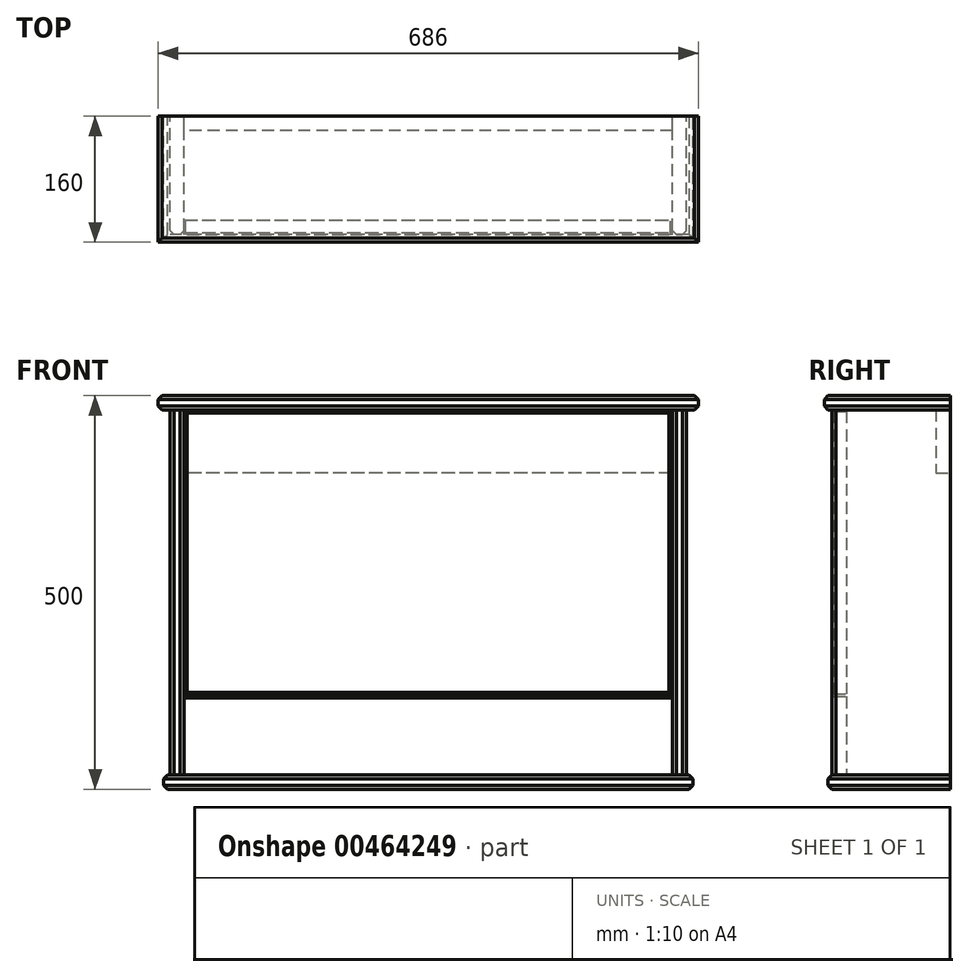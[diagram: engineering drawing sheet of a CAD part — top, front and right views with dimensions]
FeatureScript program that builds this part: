
annotation { "Feature Type Name" : "Feature", "Feature Type Description" : "" }
export const myFeature = defineFeature(function(context is Context, id is Id, definition is map)
    precondition{}
    {
        {
            assignVariable(context, id + "F0", {"name" : "wood", "anyValue" : 18});
        }
        {
            var Q0;
            Q0=qCreatedBy(makeId("Front.planeOp"),FACE);
            var sketch = newSketch(context, id + "F1", { "sketchPlane" : qUnion([Q0])});
            skLineSegment(sketch, "E0.bottom", {"start": v(-310, 482) * mm, "end": v(310, 482) * mm});
            skLineSegment(sketch, "E0.top", {"start": v(-310, 18) * mm, "end": v(310, 18) * mm});
            skLineSegment(sketch, "E0.left", {"start": v(-310, 482) * mm, "end": v(-310, 18) * mm});
            skLineSegment(sketch, "E0.right", {"start": v(310, 482) * mm, "end": v(310, 18) * mm});
            skLineSegment(sketch, "E1.bottom", {"start": v(-328, 500) * mm, "end": v(328, 500) * mm});
            skLineSegment(sketch, "E1.top", {"start": v(-328, 0) * mm, "end": v(328, 0) * mm});
            skLineSegment(sketch, "E1.left", {"start": v(-328, 482) * mm, "end": v(-328, 18) * mm});
            skLineSegment(sketch, "E1.right", {"start": v(328, 482) * mm, "end": v(328, 18) * mm});
            skLineSegment(sketch, "E2", {"start": v(-310, 482) * mm, "end": v(-328, 482) * mm});
            skLineSegment(sketch, "E3", {"start": v(310, 482) * mm, "end": v(328, 482) * mm});
            skLineSegment(sketch, "E4", {"start": v(-310, 18) * mm, "end": v(-328, 18) * mm});
            skLineSegment(sketch, "E5", {"start": v(310, 18) * mm, "end": v(328, 18) * mm});
            skLineSegment(sketch, "E6", {"start": v(-310, 118) * mm, "end": v(310, 118) * mm});
            skPoint(sketch, "E7.oppositeSnap0", {"position": v(319, 482) * mm});
            skLineSegment(sketch, "E7.bottom", {"start": v(328, 500) * mm, "end": v(343, 500) * mm});
            skLineSegment(sketch, "E7.top", {"start": v(328, 482) * mm, "end": v(343, 482) * mm});
            skLineSegment(sketch, "E7.right", {"start": v(343, 500) * mm, "end": v(343, 482) * mm});
            skLineSegment(sketch, "E8.MirrorCS", {"start": v(-328, 482) * mm, "end": v(-343, 482) * mm});
            skLineSegment(sketch, "E9.MirrorCS", {"start": v(-343, 500) * mm, "end": v(-343, 482) * mm});
            skLineSegment(sketch, "E10.MirrorCS", {"start": v(-328, 500) * mm, "end": v(-343, 500) * mm});
            skLineSegment(sketch, "E11", {"start": v(328, 18) * mm, "end": v(336, 18) * mm});
            skLineSegment(sketch, "E12", {"start": v(336, 18) * mm, "end": v(336, 0) * mm});
            skLineSegment(sketch, "E13", {"start": v(336, 0) * mm, "end": v(328, 0) * mm});
            skLineSegment(sketch, "E14.MirrorCS", {"start": v(-328, 18) * mm, "end": v(-336, 18) * mm});
            skLineSegment(sketch, "E15.MirrorCS", {"start": v(-336, 0) * mm, "end": v(-328, 0) * mm});
            skLineSegment(sketch, "E16.MirrorCS", {"start": v(-336, 18) * mm, "end": v(-336, 0) * mm});
            skLineSegment(sketch, "E17.bottom", {"start": v(-308, 480) * mm, "end": v(308, 480) * mm});
            skLineSegment(sketch, "E17.top", {"start": v(-308, 121) * mm, "end": v(308, 121) * mm});
            skLineSegment(sketch, "E17.left", {"start": v(-308, 480) * mm, "end": v(-308, 121) * mm});
            skLineSegment(sketch, "E17.right", {"start": v(308, 480) * mm, "end": v(308, 121) * mm});
            skSolve(sketch);
        }
        {
            var Q0;
            {var subQ0=sQuery(id+"F1.wireOp",EDGE,"E2");Q0=makeQuery(id+"F1.imprint","IMPRINT",FACE,{"disambiguationData":[TD([[makeQuery(id+"F1.imprint","IMPRINT",EDGE,{"derivedFrom":subQ0}),1.0]])]});}
            var Q1;
            Q1=makeQuery(id+"F1.imprint","IMPRINT",FACE,{"disambiguationData":[TD([[makeQuery(id+"F1.imprint","IMPRINT",EDGE,{"derivedFrom":sQuery(id+"F1.wireOp",EDGE,"E1.right")}),-1.0]])]});
            extrude(context, id + "F2", {"entities" : qUnion([Q0, Q1]), "depth" : 150 * mm, "offsetDistance" : 25 * mm});
        }
        {
            var Q0;
            Q0=makeQuery(id+"F1.imprint","IMPRINT",FACE,{"disambiguationData":[TD([[makeQuery(id+"F1.imprint","IMPRINT",EDGE,{"derivedFrom":sQuery(id+"F1.wireOp",EDGE,"E0.top")}),-1.0]])]});
            var Q1;
            Q1=makeQuery(id+"F2.opExtrude","CAP_FACE",FACE,{"disambiguationData":[OSD([sQuery(id+"F1.wireOp",EDGE,"E0.left"),sQuery(id+"F1.wireOp",EDGE,"E1.left"),sQuery(id+"F1.wireOp",EDGE,"E2"),sQuery(id+"F1.wireOp",EDGE,"E4")])],"isStart":false});
            extrude(context, id + "F3", {"entities" : qUnion([Q0]), "endBound" : BoundingType.UP_TO_SURFACE, "depth" : 25 * mm, "endBoundEntityFace" : qUnion([Q1]), "hasOffset" : true, "offsetDistance" : 5 * mm, "offsetOppositeDirection" : true});
        }
        {
            var Q0;
            {var subQ0=sQuery(id+"F1.wireOp",EDGE,"E0.top");Q0=makeQuery(id+"F1.imprint","IMPRINT",FACE,{"disambiguationData":[TD([[makeQuery(id+"F1.imprint","IMPRINT",EDGE,{"derivedFrom":subQ0}),1.0]])]});}
            var Q1;
            Q1=makeQuery(id+"F2.opExtrude","CAP_FACE",FACE,{"disambiguationData":[OSD([sQuery(id+"F1.wireOp",EDGE,"E0.left"),sQuery(id+"F1.wireOp",EDGE,"E1.left"),sQuery(id+"F1.wireOp",EDGE,"E2"),sQuery(id+"F1.wireOp",EDGE,"E4")])],"isStart":false});
            var Q2;
            Q2=makeQuery(id+"F2.opExtrude","CAP_FACE",FACE,{"disambiguationData":[OSD([sQuery(id+"F1.wireOp",EDGE,"E0.left"),sQuery(id+"F1.wireOp",EDGE,"E1.left"),sQuery(id+"F1.wireOp",EDGE,"E2"),sQuery(id+"F1.wireOp",EDGE,"E4")])],"isStart":false});
            extrude(context, id + "F4", {"entities" : qUnion([Q0]), "endBound" : BoundingType.UP_TO_SURFACE, "depth" : 25 * mm, "endBoundEntityFace" : qUnion([Q1]), "offsetDistance" : 25 * mm, "hasSecondDirection" : true, "secondDirectionBound" : BoundingType.UP_TO_SURFACE, "secondDirectionOppositeDirection" : false, "secondDirectionDepth" : 25 * mm, "secondDirectionBoundEntityFace" : qUnion([Q2]), "hasSecondDirectionOffset" : true, "secondDirectionOffsetDistance" : (getVariable(context, 'wood')) * mm});
        }
        {
            var Q0;
            Q0=makeQuery(id+"F1.imprint","IMPRINT",FACE,{"disambiguationData":[TD([[makeQuery(id+"F1.imprint","IMPRINT",EDGE,{"derivedFrom":sQuery(id+"F1.wireOp",EDGE,"E0.bottom")}),1.0]])]});
            var Q1;
            Q1=makeQuery(id+"F2.opExtrude","CAP_FACE",FACE,{"disambiguationData":[OSD([sQuery(id+"F1.wireOp",EDGE,"E0.left"),sQuery(id+"F1.wireOp",EDGE,"E1.left"),sQuery(id+"F1.wireOp",EDGE,"E2"),sQuery(id+"F1.wireOp",EDGE,"E4")])],"isStart":false});
            extrude(context, id + "F5", {"entities" : qUnion([Q0]), "endBound" : BoundingType.UP_TO_SURFACE, "depth" : 25 * mm, "endBoundEntityFace" : qUnion([Q1]), "hasOffset" : true, "offsetDistance" : 10 * mm, "offsetOppositeDirection" : true});
        }
        {
            var Q0;
            Q0=makeQuery(id+"F1.imprint","IMPRINT",FACE,{"disambiguationData":[TD([[makeQuery(id+"F1.imprint","IMPRINT",EDGE,{"derivedFrom":sQuery(id+"F1.wireOp",EDGE,"E17.bottom")}),-1.0]])]});
            var Q1;
            Q1=makeQuery(id+"F4.opExtrude","CAP_FACE",FACE,{"disambiguationData":[OSD([sQuery(id+"F1.wireOp",EDGE,"E0.top"),sQuery(id+"F1.wireOp",EDGE,"E0.left"),sQuery(id+"F1.wireOp",EDGE,"E0.right"),sQuery(id+"F1.wireOp",EDGE,"E6")])],"isStart":false});
            var Q2;
            Q2=makeQuery(id+"F4.opExtrude","CAP_FACE",FACE,{"disambiguationData":[OSD([sQuery(id+"F1.wireOp",EDGE,"E0.top"),sQuery(id+"F1.wireOp",EDGE,"E0.left"),sQuery(id+"F1.wireOp",EDGE,"E0.right"),sQuery(id+"F1.wireOp",EDGE,"E6")])],"isStart":false});
            extrude(context, id + "F6", {"entities" : qUnion([Q0]), "endBound" : BoundingType.UP_TO_SURFACE, "depth" : (getVariable(context, 'wood')) * mm, "endBoundEntityFace" : qUnion([Q1]), "offsetDistance" : (getVariable(context, 'wood')) * mm, "offsetOppositeDirection" : true, "hasSecondDirection" : true, "secondDirectionBound" : BoundingType.UP_TO_SURFACE, "secondDirectionOppositeDirection" : false, "secondDirectionDepth" : 25 * mm, "secondDirectionBoundEntityFace" : qUnion([Q2]), "hasSecondDirectionOffset" : true, "secondDirectionOffsetDistance" : (getVariable(context, 'wood')) * mm});
        }
        {
            var Q0;
            Q0=makeQuery(id+"F1.imprint","IMPRINT",FACE,{"disambiguationData":[TD([[makeQuery(id+"F1.imprint","IMPRINT",EDGE,{"derivedFrom":sQuery(id+"F1.wireOp",EDGE,"E17.bottom")}),-1.0]])]});
            var sketch = newSketch(context, id + "F7", { "sketchPlane" : qUnion([Q0])});
            skLineSegment(sketch, "E18.bottom", {"start": v(310, 482) * mm, "end": v(-310, 482) * mm});
            skLineSegment(sketch, "E18.top", {"start": v(310, 402) * mm, "end": v(-310, 402) * mm});
            skLineSegment(sketch, "E18.left", {"start": v(310, 482) * mm, "end": v(310, 402) * mm});
            skLineSegment(sketch, "E18.right", {"start": v(-310, 482) * mm, "end": v(-310, 402) * mm});
            skSolve(sketch);
        }
        {
            var Q0;
            Q0 = qSketchRegion(id + "F7", true);
            extrude(context, id + "F8", {"entities" : qUnion([Q0]), "depth" : (getVariable(context, 'wood')) * mm, "offsetDistance" : 25 * mm});
        }
        {
            var Q0;
            Q0=makeQuery(id+"F5.opExtrude","CAP_EDGE",EDGE,{"disambiguationData":[OSD([sQuery(id+"F1.wireOp",EDGE,"E1.bottom"),sQuery(id+"F1.wireOp",EDGE,"E7.bottom"),sQuery(id+"F1.wireOp",EDGE,"E10.MirrorCS")])],"isStart":false});
            var Q1;
            Q1=makeQuery(id+"F5.opExtrude","SWEPT_EDGE",EDGE,{"disambiguationData":[OSD([sQuery(id+"F1.wireOp",EDGE,"E9.MirrorCS"),sQuery(id+"F1.wireOp",EDGE,"E10.MirrorCS")])]});
            var Q2;
            Q2=makeQuery(id+"F5.opExtrude","SWEPT_EDGE",EDGE,{"disambiguationData":[OSD([sQuery(id+"F1.wireOp",EDGE,"E7.bottom"),sQuery(id+"F1.wireOp",EDGE,"E7.right")])]});
            var Q3;
            Q3=makeQuery(id+"F5.opExtrude","SWEPT_EDGE",EDGE,{"disambiguationData":[OSD([sQuery(id+"F1.wireOp",EDGE,"E7.top"),sQuery(id+"F1.wireOp",EDGE,"E7.right")])]});
            var Q4;
            Q4=makeQuery(id+"F5.opExtrude","CAP_EDGE",EDGE,{"disambiguationData":[OSD([sQuery(id+"F1.wireOp",EDGE,"E0.bottom"),sQuery(id+"F1.wireOp",EDGE,"E2"),sQuery(id+"F1.wireOp",EDGE,"E3"),sQuery(id+"F1.wireOp",EDGE,"E7.top"),sQuery(id+"F1.wireOp",EDGE,"E8.MirrorCS")])],"isStart":false});
            var Q5;
            Q5=makeQuery(id+"F5.opExtrude","SWEPT_EDGE",EDGE,{"disambiguationData":[OSD([sQuery(id+"F1.wireOp",EDGE,"E8.MirrorCS"),sQuery(id+"F1.wireOp",EDGE,"E9.MirrorCS")])]});
            var Q6;
            Q6=makeQuery(id+"F2.opExtrude","CAP_EDGE",EDGE,{"disambiguationData":[OSD([sQuery(id+"F1.wireOp",EDGE,"E1.left")])],"isStart":false});
            var Q7;
            Q7=makeQuery(id+"F2.opExtrude","CAP_EDGE",EDGE,{"disambiguationData":[OSD([sQuery(id+"F1.wireOp",EDGE,"E0.left")])],"isStart":false});
            var Q8;
            Q8=makeQuery(id+"F2.opExtrude","CAP_EDGE",EDGE,{"disambiguationData":[OSD([sQuery(id+"F1.wireOp",EDGE,"E0.right")])],"isStart":false});
            var Q9;
            Q9=makeQuery(id+"F2.opExtrude","CAP_EDGE",EDGE,{"disambiguationData":[OSD([sQuery(id+"F1.wireOp",EDGE,"E1.right")])],"isStart":false});
            var Q10;
            Q10=makeQuery(id+"F3.opExtrude","CAP_EDGE",EDGE,{"disambiguationData":[OSD([sQuery(id+"F1.wireOp",EDGE,"E0.top"),sQuery(id+"F1.wireOp",EDGE,"E4"),sQuery(id+"F1.wireOp",EDGE,"E5")])],"isStart":false});
            var Q11;
            Q11=makeQuery(id+"F3.opExtrude","CAP_EDGE",EDGE,{"disambiguationData":[OSD([sQuery(id+"F1.wireOp",EDGE,"E1.top")])],"isStart":false});
            var Q12;
            Q12=makeQuery(id+"F3.opExtrude","SWEPT_EDGE",EDGE,{"disambiguationData":[OSD([sQuery(id+"F1.wireOp",EDGE,"E1.top"),sQuery(id+"F1.wireOp",EDGE,"XIpwYMWb-v9uu-UivI-sULC-HTFqOk4br6iA")])]});
            var Q13;
            Q13=makeQuery(id+"F3.opExtrude","SWEPT_EDGE",EDGE,{"disambiguationData":[OSD([sQuery(id+"F1.wireOp",EDGE,"E1.top"),sQuery(id+"F1.wireOp",EDGE,"E1.left")])]});
            var Q14;
            Q14=makeQuery(id+"F3.opExtrude","SWEPT_EDGE",EDGE,{"disambiguationData":[OSD([sQuery(id+"F1.wireOp",EDGE,"E11"),sQuery(id+"F1.wireOp",EDGE,"E12")])]});
            var Q15;
            Q15=makeQuery(id+"F3.opExtrude","SWEPT_EDGE",EDGE,{"disambiguationData":[OSD([sQuery(id+"F1.wireOp",EDGE,"E12"),sQuery(id+"F1.wireOp",EDGE,"E13")])]});
            var Q16;
            Q16=makeQuery(id+"F3.opExtrude","SWEPT_EDGE",EDGE,{"disambiguationData":[OSD([sQuery(id+"F1.wireOp",EDGE,"E15.MirrorCS"),sQuery(id+"F1.wireOp",EDGE,"E16.MirrorCS")])]});
            var Q17;
            Q17=makeQuery(id+"F3.opExtrude","SWEPT_EDGE",EDGE,{"disambiguationData":[OSD([sQuery(id+"F1.wireOp",EDGE,"E14.MirrorCS"),sQuery(id+"F1.wireOp",EDGE,"E16.MirrorCS")])]});
            chamfer(context, id + "F9", {"entities" : qUnion([Q0, Q1, Q2, Q3, Q4, Q5, Q6, Q7, Q8, Q9, Q10, Q11, Q12, Q13, Q14, Q15, Q16, Q17]), "width" : 5 * mm, "tangentPropagation" : true});
        }
        {
            var Q0;
            Q0=makeQuery(id+"F6.opExtrude","CAP_FACE",FACE,{"disambiguationData":[OSD([sQuery(id+"F1.wireOp",EDGE,"E17.bottom"),sQuery(id+"F1.wireOp",EDGE,"E17.top"),sQuery(id+"F1.wireOp",EDGE,"E17.left"),sQuery(id+"F1.wireOp",EDGE,"E17.right")])],"isStart":false});
            var Q1;
            Q1=makeQuery(id+"F4.opExtrude","CAP_EDGE",EDGE,{"disambiguationData":[OSD([sQuery(id+"F1.wireOp",EDGE,"E6")])],"isStart":false});
            chamfer(context, id + "F10", {"entities" : qUnion([Q0, Q1]), "width" : 2 * mm, "tangentPropagation" : true});
        }
    });
